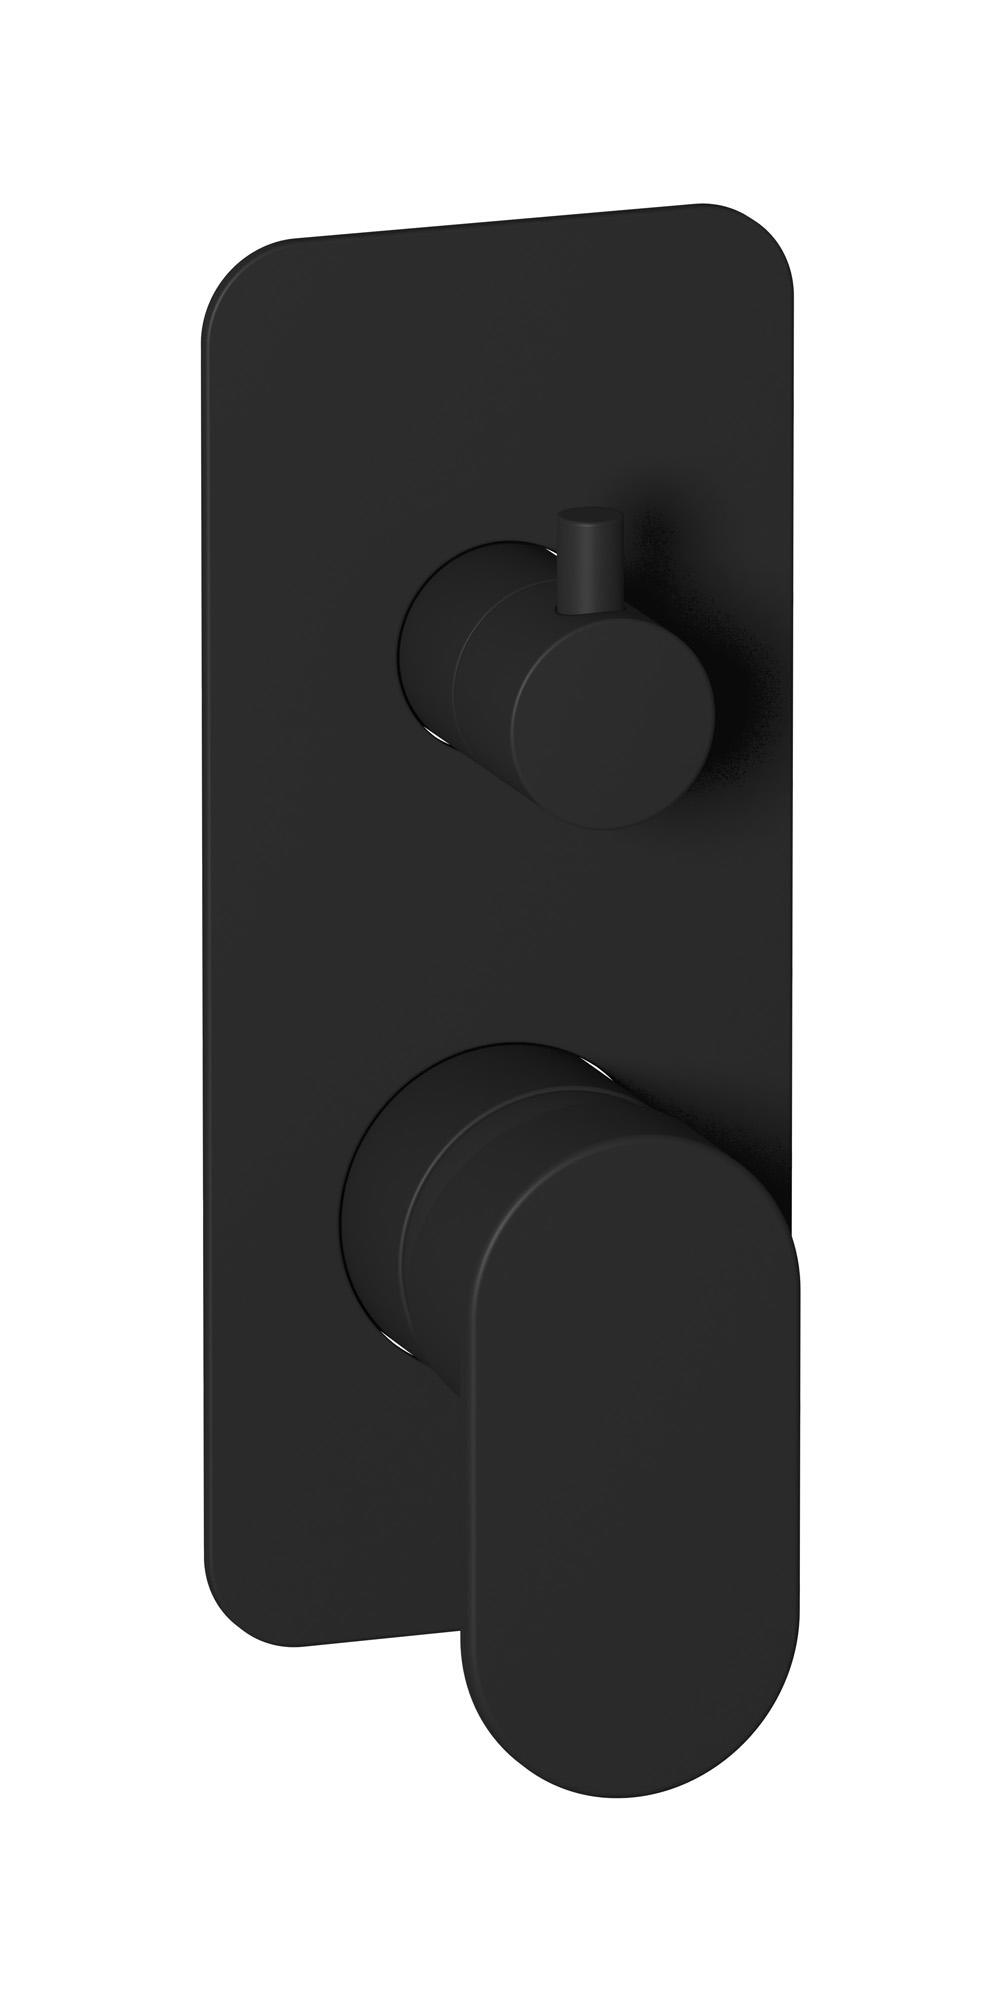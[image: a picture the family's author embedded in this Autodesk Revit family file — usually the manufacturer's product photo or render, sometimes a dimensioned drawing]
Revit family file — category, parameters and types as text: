
# Revit family: LM312
name_source: partatom
category: Apparecchi idraulici
units: mm (PartAtom-declared; Revit-internal decimal feet)

## family parameters
Basato su piano di lavoro = No
Condiviso = No
Mantieni orientamento annotazione = No
Numero OmniClass = 23.45.55.17
Punto di calcolo locali = No
Quota connettore circolare = Usa diametro
Sempre verticale = Sì
Taglio con vuoti quando caricato = No
Tipo di parte = Normale
Titolo OmniClass = Mixing Faucets

## types (9) — shared parameters
Cold water inlet = 10 mm  [stored 0.0328084 ft]
Commenti sul tipo = Wall mixer
Connessione CW = No
Connessione HW = No
Connessione di scarico = No
Connessione di ventilazione = No
Descrizione = Exposed parts for manual wall mixer with three ways diverter
Hot water inlet = 10 mm  [stored 0.0328084 ft]
Produttore = IB Rubinetterie S.p.A.
URL = https://www.weareib.it
zero-valued in all types: Prospetto di default

## per-type parameters (varying)
| type | Finishes surface | Immagine tipo | Modello |
| Chrome | IB_Chrome | LM312CC.jpg | LM312CC |
| Brushed nickel | IB_Brushed nickel | LM312SS.jpg | LM312SS |
| Matt black | IB_matt black | LM312NP.jpg | LM312NP |
| Matt white | IB_matt white | LM312BO.jpg | LM312BO |
| Natural brass | IB_Brass | LM312ON.jpg | LM312ON |
| Brushed black chrome | IB_Brushed black chrome | LM312CS.jpg | LM312CS |
| Brushed pale gold | IB_brushed pale gold | LM312IS.jpg | LM312IS |
| Brushed gold | IB_brushed gold | LM312OS.jpg | LM312OS |
| Brushed rose gold | IB_Brushed rose gold | LM312SR.jpg | LM312RS |

note: [stored X ft] marks values corroborated as IEEE doubles in the binary element streams (Revit-internal decimal feet)
